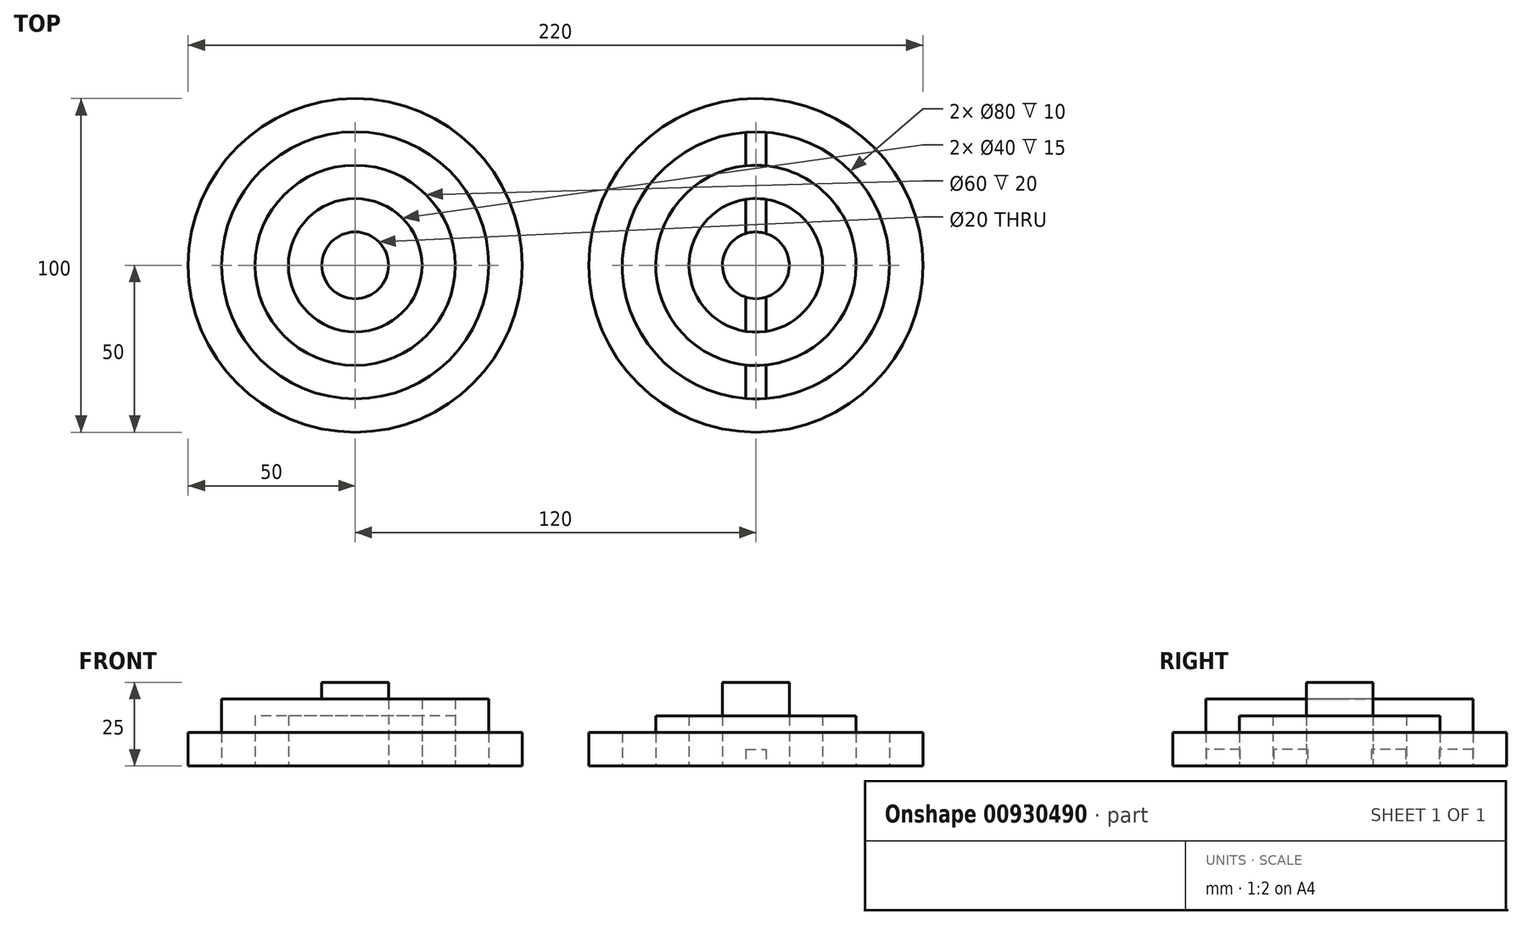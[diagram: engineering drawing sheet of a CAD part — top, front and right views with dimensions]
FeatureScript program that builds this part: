
annotation { "Feature Type Name" : "Feature", "Feature Type Description" : "" }
export const myFeature = defineFeature(function(context is Context, id is Id, definition is map)
    precondition{}
    {
        {
            var Q0;
            Q0=qCreatedBy(makeId("Top.planeOp"),FACE);
            var sketch = newSketch(context, id + "F0", { "sketchPlane" : qUnion([Q0])});
            skCircle(sketch, "E0", {"center": v(0, 0) * mm, "radius": 10 * mm});
            skCircle(sketch, "E1", {"center": v(0, 0) * mm, "radius": 20 * mm});
            skCircle(sketch, "E2", {"center": v(0, 0) * mm, "radius": 30 * mm});
            skCircle(sketch, "E3", {"center": v(0, 0) * mm, "radius": 40 * mm});
            skCircle(sketch, "E4", {"center": v(0, 0) * mm, "radius": 50 * mm});
            skSolve(sketch);
        }
        {
            var Q0;
            Q0=qCreatedBy(makeId("Top.planeOp"),FACE);
            var sketch = newSketch(context, id + "F1", { "sketchPlane" : qUnion([Q0])});
            skLineSegment(sketch, "E5", {"start": v(0, 0) * mm, "end": v(120, 0) * mm, "construction": true});
            skCircle(sketch, "E6", {"center": v(120, 0) * mm, "radius": 40 * mm});
            skCircle(sketch, "E7", {"center": v(120, 0) * mm, "radius": 30 * mm});
            skCircle(sketch, "E8", {"center": v(120, 0) * mm, "radius": 20 * mm});
            skCircle(sketch, "E9", {"center": v(120, 0) * mm, "radius": 10 * mm});
            skCircle(sketch, "E10", {"center": v(120, 0) * mm, "radius": 50 * mm});
            skSolve(sketch);
        }
        {
            var Q0;
            Q0=makeQuery(id+"F0.imprint","IMPRINT",FACE,{"disambiguationData":[TD([[makeQuery(id+"F0.imprint","IMPRINT",EDGE,{"derivedFrom":sQuery(id+"F0.wireOp",EDGE,"E3")}),-1.0]])]});
            extrude(context, id + "F2", {"entities" : qUnion([Q0]), "depth" : 10 * mm, "offsetDistance" : 25 * mm});
        }
        {
            var Q0;
            Q0=makeQuery(id+"F0.imprint","IMPRINT",FACE,{"disambiguationData":[TD([[makeQuery(id+"F0.imprint","IMPRINT",EDGE,{"derivedFrom":sQuery(id+"F0.wireOp",EDGE,"E1")}),-1.0]])]});
            extrude(context, id + "F3", {"entities" : qUnion([Q0]), "depth" : 15 * mm, "offsetDistance" : 25 * mm});
        }
        {
            var Q0;
            Q0=makeQuery(id+"F0.imprint","IMPRINT",FACE,{"disambiguationData":[TD([[makeQuery(id+"F0.imprint","IMPRINT",EDGE,{"derivedFrom":sQuery(id+"F0.wireOp",EDGE,"E0")}),1.0]])]});
            extrude(context, id + "F4", {"entities" : qUnion([Q0]), "depth" : 25 * mm, "offsetDistance" : 25 * mm});
        }
        {
            var Q0;
            Q0=makeQuery(id+"F1.imprint","IMPRINT",FACE,{"disambiguationData":[TD([[makeQuery(id+"F1.imprint","IMPRINT",EDGE,{"derivedFrom":sQuery(id+"F1.wireOp",EDGE,"E6")}),-1.0]])]});
            extrude(context, id + "F5", {"entities" : qUnion([Q0]), "depth" : 10 * mm, "offsetDistance" : 25 * mm});
        }
        {
            var Q0;
            Q0=makeQuery(id+"F1.imprint","IMPRINT",FACE,{"disambiguationData":[TD([[makeQuery(id+"F1.imprint","IMPRINT",EDGE,{"derivedFrom":sQuery(id+"F1.wireOp",EDGE,"E7")}),1.0]])]});
            extrude(context, id + "F6", {"entities" : qUnion([Q0]), "operationType" : NewBodyOperationType.ADD, "depth" : 15 * mm, "offsetDistance" : 25 * mm});
        }
        {
            var Q0;
            Q0=makeQuery(id+"F1.imprint","IMPRINT",FACE,{"disambiguationData":[TD([[makeQuery(id+"F1.imprint","IMPRINT",EDGE,{"derivedFrom":sQuery(id+"F1.wireOp",EDGE,"E9")}),1.0]])]});
            extrude(context, id + "F7", {"entities" : qUnion([Q0]), "operationType" : NewBodyOperationType.ADD, "depth" : 25 * mm, "offsetDistance" : 25 * mm});
        }
        {
            var Q0;
            Q0=qCreatedBy(makeId("Top.planeOp"),FACE);
            var sketch = newSketch(context, id + "F8", { "sketchPlane" : qUnion([Q0])});
            skLineSegment(sketch, "E11.bottom", {"start": v(117, 0) * mm, "end": v(123, 0) * mm});
            skLineSegment(sketch, "E11.top", {"start": v(117, -49.9) * mm, "end": v(123, -49.9) * mm});
            skLineSegment(sketch, "E11.left", {"start": v(117, 49.9) * mm, "end": v(117, -49.9) * mm});
            skLineSegment(sketch, "E11.right", {"start": v(123, 49.9) * mm, "end": v(123, -49.9) * mm});
            skLineSegment(sketch, "E12", {"start": v(120, 0) * mm, "end": v(120, -49.9) * mm, "construction": true});
            skLineSegment(sketch, "E13", {"start": v(117, 49.9) * mm, "end": v(123, 49.9) * mm});
            skSolve(sketch);
        }
        {
            var Q0;
            Q0 = qSketchRegion(id + "F8", true);
            extrude(context, id + "F9", {"entities" : qUnion([Q0]), "operationType" : NewBodyOperationType.ADD, "depth" : 5 * mm, "offsetDistance" : 25 * mm});
        }
        {
            var Q0;
            Q0=makeQuery(id+"F0.imprint","IMPRINT",FACE,{"disambiguationData":[TD([[makeQuery(id+"F0.imprint","IMPRINT",EDGE,{"derivedFrom":sQuery(id+"F0.wireOp",EDGE,"E2")}),-1.0]])]});
            var Q1;
            Q1=makeQuery(id+"F0.imprint","IMPRINT",FACE,{"disambiguationData":[TD([[makeQuery(id+"F0.imprint","IMPRINT",EDGE,{"derivedFrom":sQuery(id+"F0.wireOp",EDGE,"E0")}),-1.0]])]});
            extrude(context, id + "F10", {"entities" : qUnion([Q0, Q1]), "depth" : 20 * mm, "offsetDistance" : 25 * mm});
        }
    });
